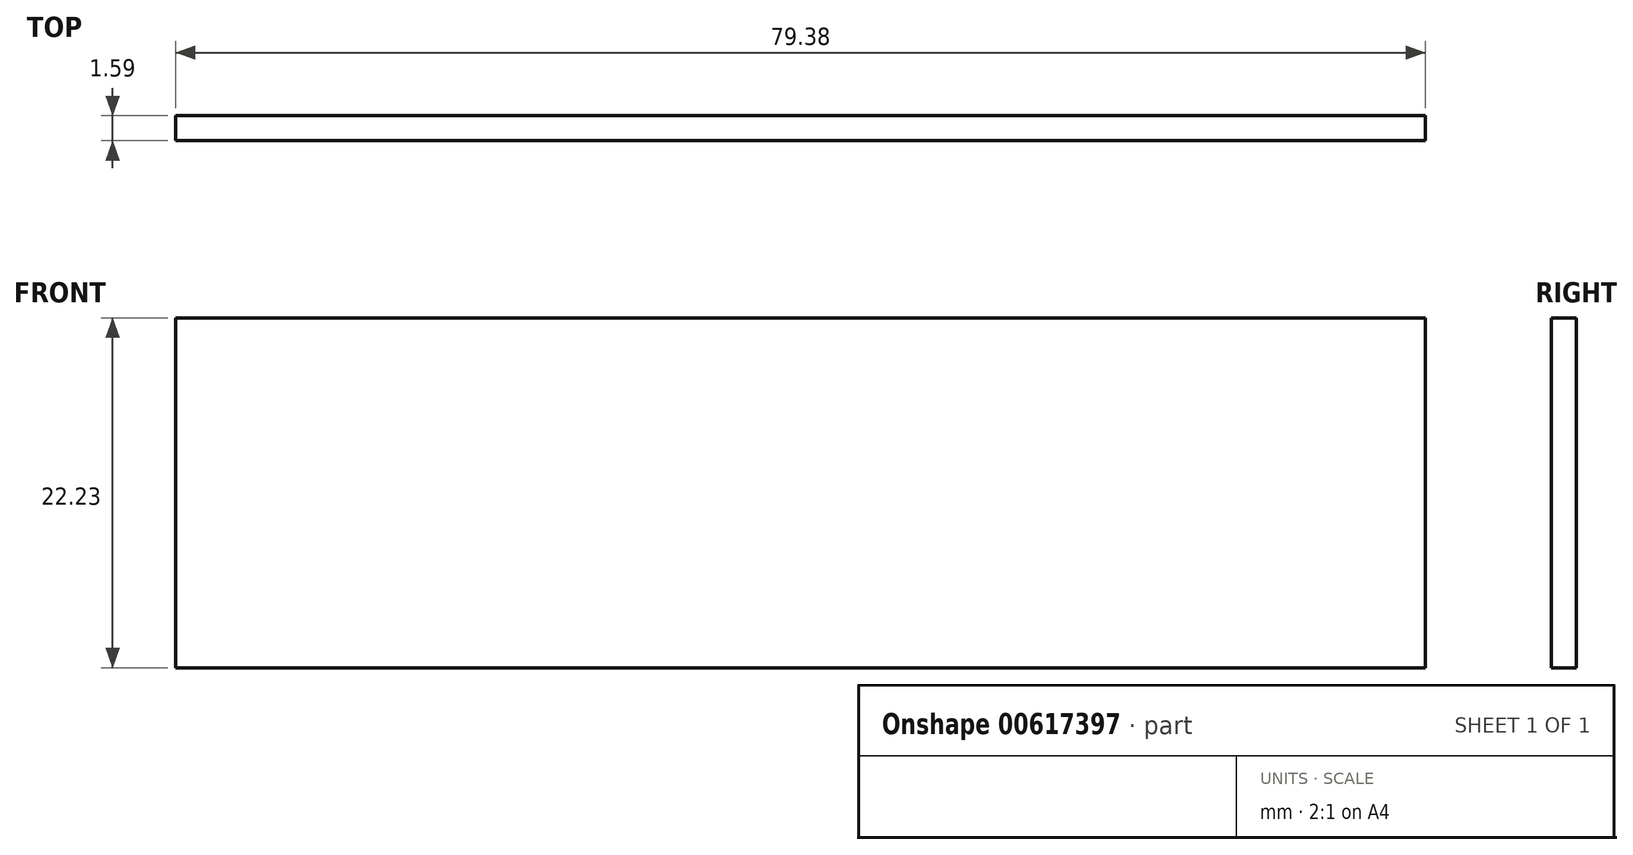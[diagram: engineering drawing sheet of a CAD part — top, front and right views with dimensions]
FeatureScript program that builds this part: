
annotation { "Feature Type Name" : "Feature", "Feature Type Description" : "" }
export const myFeature = defineFeature(function(context is Context, id is Id, definition is map)
    precondition{}
    {
        {
            var Q0;
            Q0=qCreatedBy(makeId("Front.planeOp"),FACE);
            var sketch = newSketch(context, id + "F0", { "sketchPlane" : qUnion([Q0])});
            skLineSegment(sketch, "E0.bottom", {"start": v(0, 0) * mm, "end": v(79.38, 0) * mm});
            skLineSegment(sketch, "E0.top", {"start": v(0, 22.22) * mm, "end": v(79.38, 22.22) * mm});
            skLineSegment(sketch, "E0.left", {"start": v(0, 0) * mm, "end": v(0, 22.22) * mm});
            skLineSegment(sketch, "E0.right", {"start": v(79.38, 0) * mm, "end": v(79.38, 22.22) * mm});
            skSolve(sketch);
        }
        {
            var Q0;
            Q0 = qSketchRegion(id + "F0", true);
            extrude(context, id + "F1", {"entities" : qUnion([Q0]), "depth" : 1.59 * mm, "offsetDistance" : 25.4 * mm});
        }
    });
